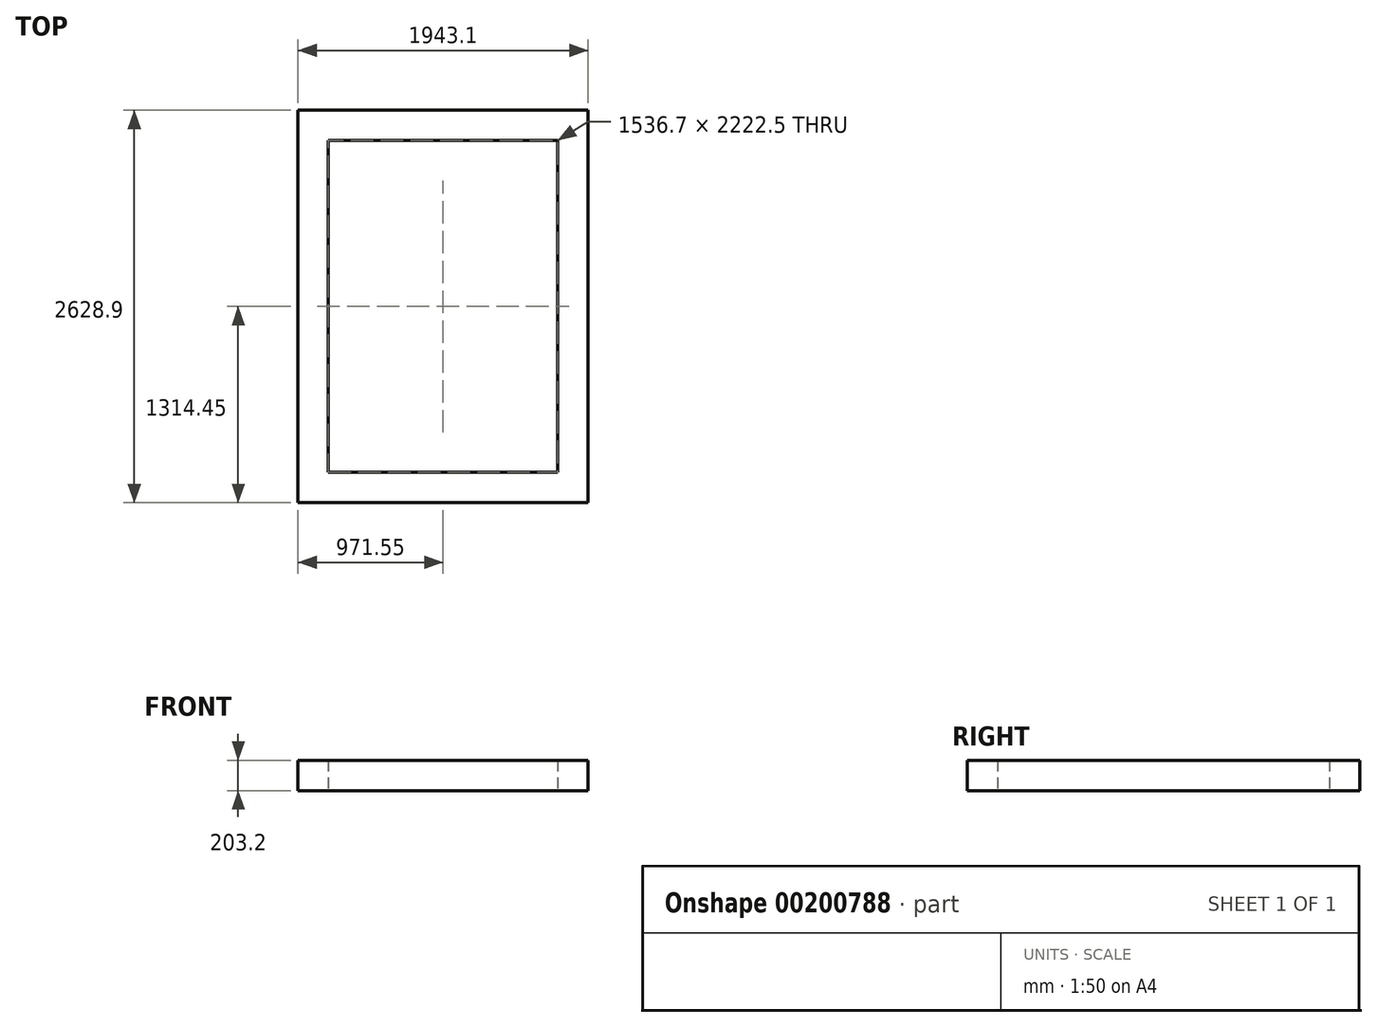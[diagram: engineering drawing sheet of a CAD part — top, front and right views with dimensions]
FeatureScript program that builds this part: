
annotation { "Feature Type Name" : "Feature", "Feature Type Description" : "" }
export const myFeature = defineFeature(function(context is Context, id is Id, definition is map)
    precondition{}
    {
        {
            var Q0;
            Q0=qCreatedBy(makeId("Top.planeOp"),FACE);
            var sketch = newSketch(context, id + "F0", { "sketchPlane" : qUnion([Q0])});
            skLineSegment(sketch, "E0", {"start": v(971.55, 1314.45) * mm, "end": v(-971.55, 1314.45) * mm});
            skLineSegment(sketch, "E1", {"start": v(-971.55, 1314.45) * mm, "end": v(-971.55, -1314.45) * mm});
            skLineSegment(sketch, "E2", {"start": v(-971.55, -1314.45) * mm, "end": v(971.55, -1314.45) * mm});
            skLineSegment(sketch, "E3", {"start": v(971.55, 1314.45) * mm, "end": v(971.55, -1314.45) * mm});
            skLineSegment(sketch, "E4.0", {"start": v(768.35, 1111.25) * mm, "end": v(-768.35, 1111.25) * mm});
            skLineSegment(sketch, "E4.1", {"start": v(768.35, 1111.25) * mm, "end": v(768.35, -1111.25) * mm});
            skLineSegment(sketch, "E4.2", {"start": v(-768.35, -1111.25) * mm, "end": v(768.35, -1111.25) * mm});
            skLineSegment(sketch, "E4.3", {"start": v(-768.35, 1111.25) * mm, "end": v(-768.35, -1111.25) * mm});
            skLineSegment(sketch, "E5", {"start": v(-768.35, 1111.25) * mm, "end": v(-971.55, 1111.25) * mm});
            skLineSegment(sketch, "E6", {"start": v(768.35, 1111.25) * mm, "end": v(971.55, 1111.25) * mm});
            skLineSegment(sketch, "E7", {"start": v(-768.35, -1111.25) * mm, "end": v(-971.55, -1111.25) * mm});
            skLineSegment(sketch, "E8", {"start": v(768.35, -1111.25) * mm, "end": v(971.55, -1111.25) * mm});
            skSolve(sketch);
        }
        {
            var Q0;
            {var subQ1=sQuery(id+"F0.wireOp",EDGE,"E0");Q0=makeQuery(id+"F0.imprint","IMPRINT",FACE,{"disambiguationData":[TD([[makeQuery(id+"F0.imprint","IMPRINT",EDGE,{"derivedFrom":subQ1}),1.0]])]});}
            var Q1;
            Q1=makeQuery(id+"F0.imprint","IMPRINT",FACE,{"disambiguationData":[TD([[makeQuery(id+"F0.imprint","IMPRINT",EDGE,{"derivedFrom":sQuery(id+"F0.wireOp",EDGE,"E4.1")}),1.0]])]});
            var Q2;
            {var subQ0=sQuery(id+"F0.wireOp",EDGE,"E2");Q2=makeQuery(id+"F0.imprint","IMPRINT",FACE,{"disambiguationData":[TD([[makeQuery(id+"F0.imprint","IMPRINT",EDGE,{"derivedFrom":subQ0}),1.0]])]});}
            var Q3;
            Q3=makeQuery(id+"F0.imprint","IMPRINT",FACE,{"disambiguationData":[TD([[makeQuery(id+"F0.imprint","IMPRINT",EDGE,{"derivedFrom":sQuery(id+"F0.wireOp",EDGE,"E4.3")}),-1.0]])]});
            extrude(context, id + "F1", {"entities" : qUnion([Q0, Q1, Q2, Q3]), "depth" : 203.2 * mm});
        }
    });
